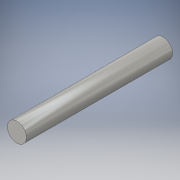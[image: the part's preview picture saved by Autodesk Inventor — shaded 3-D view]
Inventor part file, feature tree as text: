
AUTODESK INVENTOR PART (.ipt)
format: ipt  version: 2016 (Build 200138000, 138)  size: 91,648 bytes
history: native  units: in
note: dims shown in document units (in); Inventor stores cm internally (conversion verified against a paired STEP export)
features: extrude x1, sketch x1
ambient origin geometry x8: Origin, YZ Plane, XZ Plane, XY Plane, X Axis, Y Axis, Z Axis, Center Point
bodies: Solid1 (feature_tree)
feature tree (2):
  extrude  "Extrusion1"  Depth=0.9055in TaperAngle=0.0deg
  sketch  "Sketch1"  dims[d0=0.1181in d1=0.9055in d2=0.0in]
